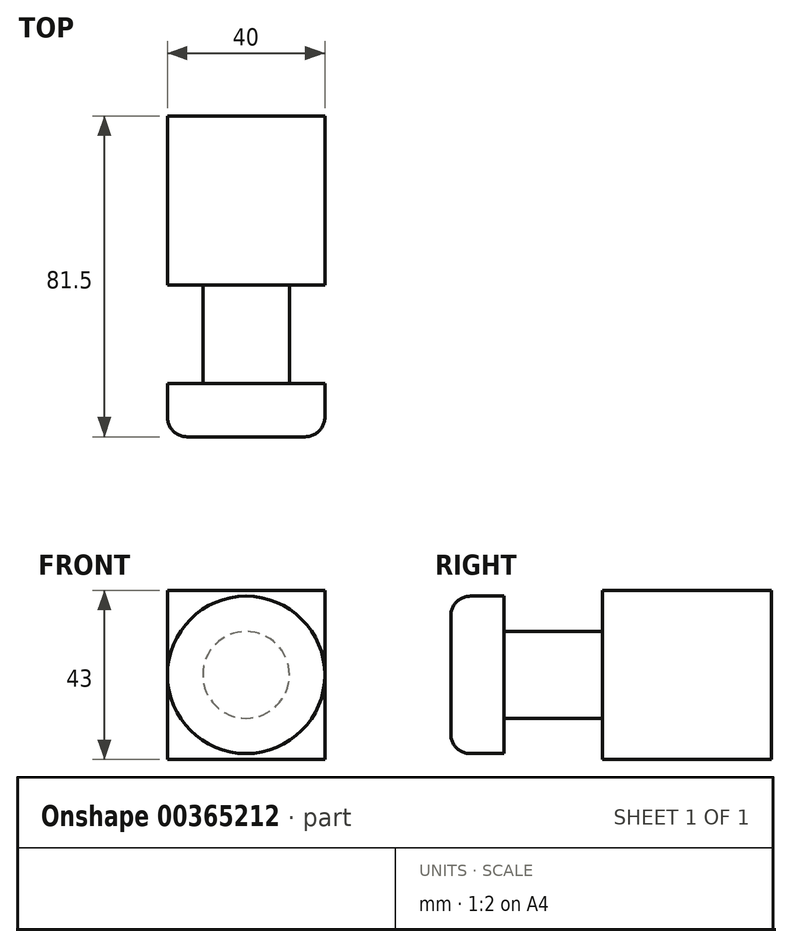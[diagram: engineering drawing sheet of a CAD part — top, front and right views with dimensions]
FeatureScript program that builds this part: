
annotation { "Feature Type Name" : "Feature", "Feature Type Description" : "" }
export const myFeature = defineFeature(function(context is Context, id is Id, definition is map)
    precondition{}
    {
        {
            var Q0;
            Q0=qCreatedBy(makeId("Front.planeOp"),FACE);
            var sketch = newSketch(context, id + "F0", { "sketchPlane" : qUnion([Q0])});
            skCircle(sketch, "E0", {"center": v(0, 0) * mm, "radius": 20 * mm});
            skSolve(sketch);
        }
        {
            var Q0;
            Q0 = qSketchRegion(id + "F0", true);
            extrude(context, id + "F1", {"entities" : qUnion([Q0]), "depth" : 38.5 * mm});
        }
        {
            var Q0;
            Q0=makeQuery(id+"F1.opExtrude","CAP_FACE",FACE,{"disambiguationData":[OSD([sQuery(id+"F0.wireOp",EDGE,"E0")])],"isStart":true});
            var sketch = newSketch(context, id + "F2", { "sketchPlane" : qUnion([Q0])});
            skLineSegment(sketch, "E1.bottom", {"start": v(20, 21.5) * mm, "end": v(-20, 21.5) * mm});
            skLineSegment(sketch, "E1.top", {"start": v(20, -21.5) * mm, "end": v(-20, -21.5) * mm});
            skLineSegment(sketch, "E1.left", {"start": v(20, 21.5) * mm, "end": v(20, -21.5) * mm});
            skLineSegment(sketch, "E1.right", {"start": v(-20, 21.5) * mm, "end": v(-20, -21.5) * mm});
            skPoint(sketch, "E1.middle", {"position": v(0, 0) * mm});
            skSolve(sketch);
        }
        {
            var Q0;
            Q0 = qSketchRegion(id + "F2", true);
            extrude(context, id + "F3", {"entities" : qUnion([Q0]), "operationType" : NewBodyOperationType.ADD, "depth" : 43 * mm});
        }
        {
            var Q0;
            {var subQ0=sQuery(id+"F2.wireOp",EDGE,"E1.left");var subQ1=sQuery(id+"F2.wireOp",EDGE,"E1.right");var subQ2=sQuery(id+"F2.wireOp",EDGE,"E1.bottom");var subQ3=makeQuery(id+"F3.opExtrude","CAP_FACE",FACE,{"disambiguationData":[OSD([subQ2,sQuery(id+"F2.wireOp",EDGE,"E1.top"),subQ0,subQ1])],"isStart":true});Q0=makeQuery(id+"F3.boolean.opBoolean","SPLIT",FACE,{"disambiguationData":[TD([makeQuery(id+"F3.opExtrude","SWEPT_FACE",FACE,{"disambiguationData":[OSD([subQ2])]})])],"derivedFrom":subQ3});}
            var sketch = newSketch(context, id + "F4", { "sketchPlane" : qUnion([Q0])});
            skCircle(sketch, "E2", {"center": v(0, 0) * mm, "radius": 11 * mm});
            skCircle(sketch, "E3.0", {"center": v(0, 0) * mm, "radius": 20 * mm});
            skSolve(sketch);
        }
        {
            var Q0;
            Q0 = qSketchRegion(id + "F4", true);
            extrude(context, id + "F5", {"entities" : qUnion([Q0]), "operationType" : NewBodyOperationType.REMOVE, "depth" : 25 * mm});
        }
        {
            var Q0;
            Q0=makeQuery(id+"F1.opExtrude","CAP_FACE",FACE,{"disambiguationData":[OSD([sQuery(id+"F0.wireOp",EDGE,"E0")])],"isStart":false});
            fillet(context, id + "F6", {"entities" : qUnion([Q0]), "radius" : 5 * mm, "tangentPropagation" : true, "allowEdgeOverflow" : false});
        }
    });
